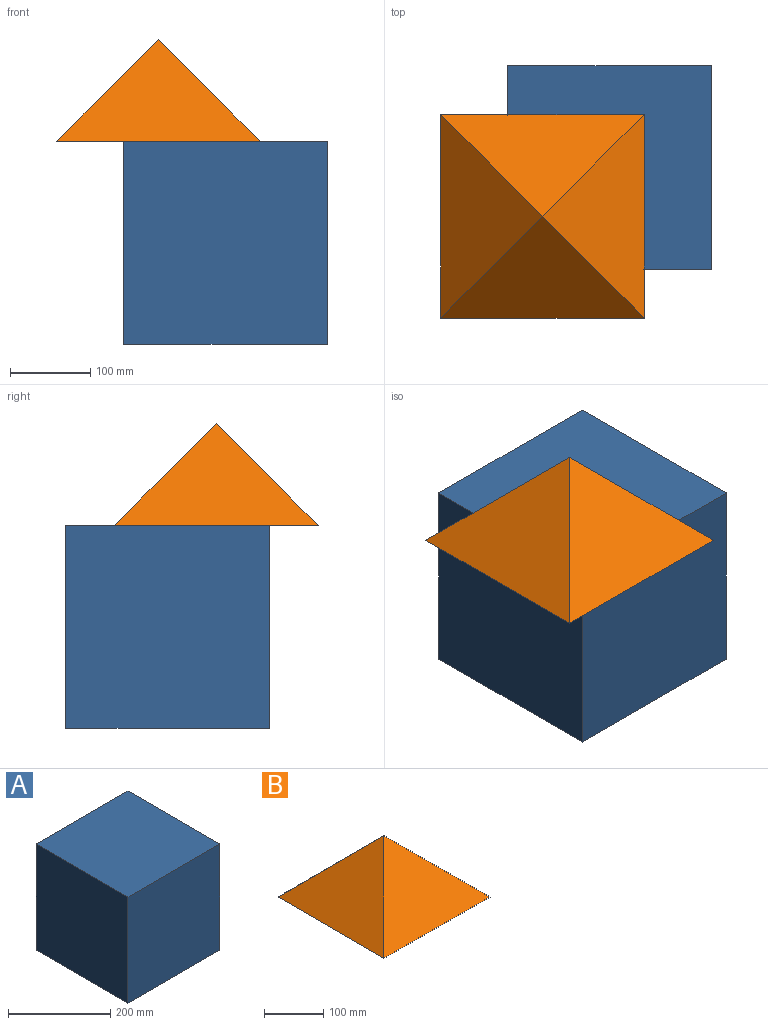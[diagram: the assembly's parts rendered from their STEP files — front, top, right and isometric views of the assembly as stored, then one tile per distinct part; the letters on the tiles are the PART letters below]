
ASSEMBLY  parts=2 mates=1
PART A: 6 faces, bbox 254x254x254 mm
  f0: plane 254x254mm, normal (0,-1,0), area 64516mm2, adj f1,f2,f3,f4
  f1: plane 254x254mm, normal (0,0,-1), area 64516mm2, adj f0,f2,f4,f5
  f2: plane 254x254mm, normal (-1,0,0), area 64516mm2, adj f0,f1,f3,f5
  f3: plane 254x254mm, normal (0,0,1), area 64516mm2, adj f0,f2,f4,f5
  f4: plane 254x254mm, normal (1,0,0), area 64516mm2, adj f0,f1,f3,f5
  f5: plane 254x254mm, normal (0,1,0), area 64516mm2, adj f1,f2,f3,f4
PART B: 5 faces, bbox 254x254x127 mm
  f0: plane 254x127mm, normal (-0.71,0,0.71), area 22809.9mm2, adj f1,f3,f4
  f1: plane 254x127mm, normal (0,-0.71,0.71), area 22809.9mm2, adj f0,f2,f4
  f2: plane 254x127mm, normal (0.71,0,0.71), area 22809.9mm2, adj f1,f3,f4
  f3: plane 254x127mm, normal (0,0.71,0.71), area 22809.9mm2, adj f0,f2,f4
  f4: plane 254x254mm, normal (0,0,-1), area 64516mm2, adj f0,f1,f2,f3
PLACE A rot(axis=(0.58,0.58,0.58),120deg) t=(11.53,89.39,-100.65)mm
PLACE B t=(54.77,28.36,26.35)mm
MATE planar A.f5 <-> B.f4  axis (0,0,1) through (138.53,89.39,26.35)mm
